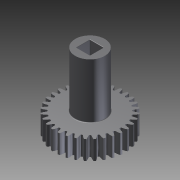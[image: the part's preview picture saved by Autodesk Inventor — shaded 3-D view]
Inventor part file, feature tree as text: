
AUTODESK INVENTOR PART (.ipt)
format: ipt  version: 2013 (Build 170138000, 138)  size: 913,408 bytes
history: native  units: mm
features: fillet x1, imported_body x1
ambient origin geometry x8: Origin, YZ Plane, XZ Plane, XY Plane, X Axis, Y Axis, Z Axis, Center Point
feature tree (2):
  fillet  "Fillet2"  [1 undecoded]
  imported_body  "Base1"
note: 1 required parameter value undecoded (feature->parameter linkage not recoverable at this tier; creation-order binding heuristic only, values carry confidence <= 0.55)
